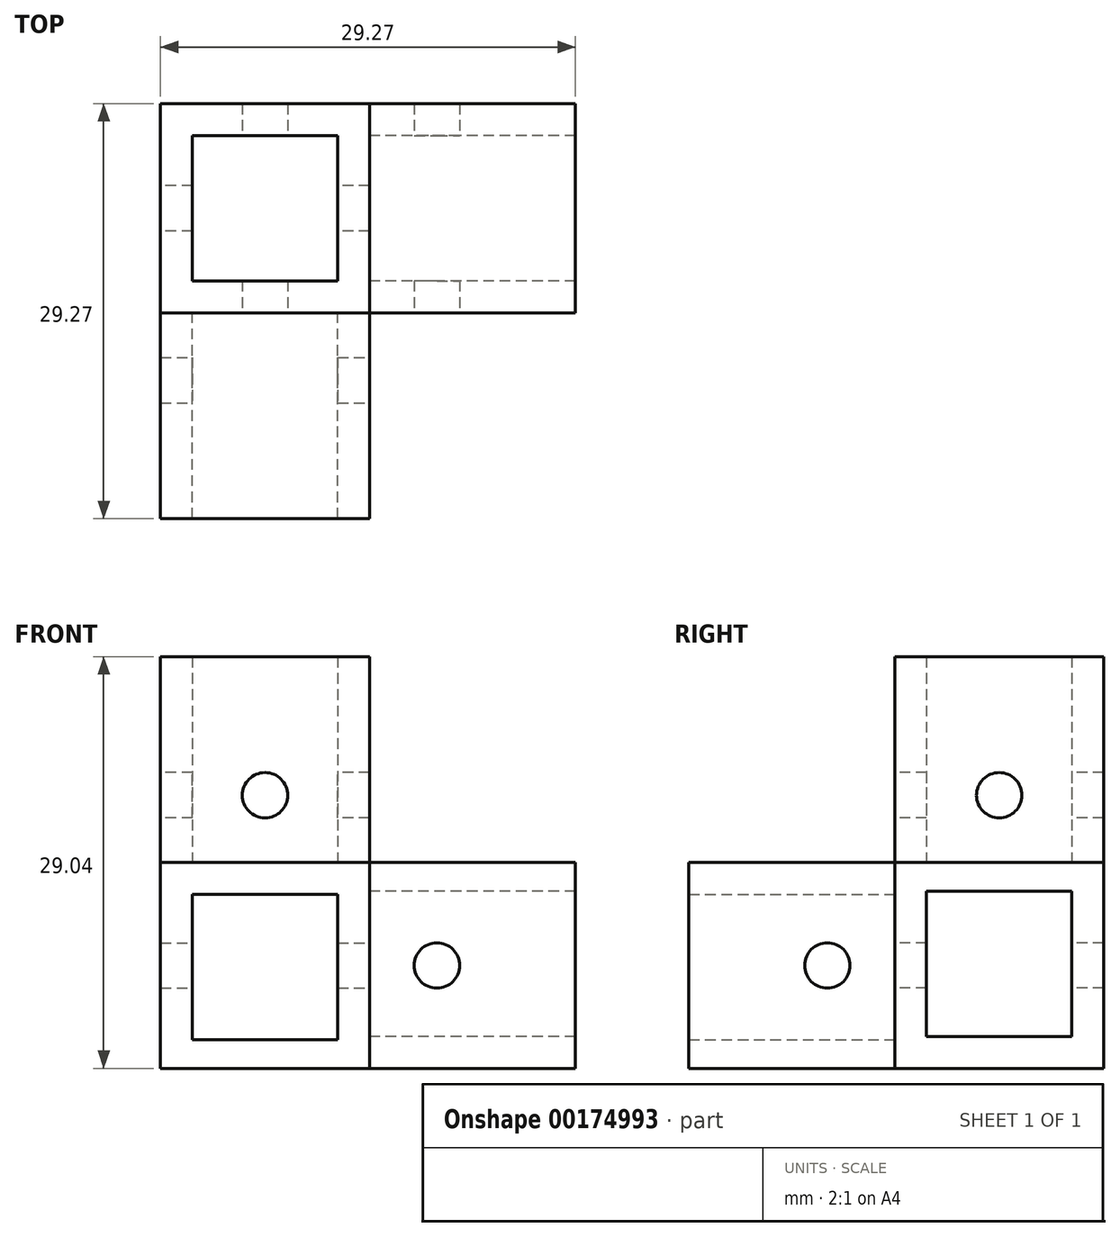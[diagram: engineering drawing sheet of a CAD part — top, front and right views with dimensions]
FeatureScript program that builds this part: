
annotation { "Feature Type Name" : "Feature", "Feature Type Description" : "" }
export const myFeature = defineFeature(function(context is Context, id is Id, definition is map)
    precondition{}
    {
        {
            var Q0;
            Q0=qCreatedBy(makeId("Top.planeOp"),FACE);
            var sketch = newSketch(context, id + "F0", { "sketchPlane" : qUnion([Q0])});
            skLineSegment(sketch, "E0.bottom", {"start": v(0, 0) * mm, "end": v(10.25, 0) * mm});
            skLineSegment(sketch, "E0.top", {"start": v(0, -10.25) * mm, "end": v(10.25, -10.25) * mm});
            skLineSegment(sketch, "E0.left", {"start": v(0, 0) * mm, "end": v(0, -10.25) * mm});
            skLineSegment(sketch, "E0.right", {"start": v(10.25, 0) * mm, "end": v(10.25, -10.25) * mm});
            skLineSegment(sketch, "E1.bottom", {"start": v(-2.25, 2.25) * mm, "end": v(12.5, 2.25) * mm});
            skLineSegment(sketch, "E1.top", {"start": v(-2.25, -12.5) * mm, "end": v(12.5, -12.5) * mm});
            skLineSegment(sketch, "E1.left", {"start": v(-2.25, 2.25) * mm, "end": v(-2.25, -12.5) * mm});
            skLineSegment(sketch, "E1.right", {"start": v(12.5, 2.25) * mm, "end": v(12.5, -12.5) * mm});
            skSolve(sketch);
        }
        {
            var Q0;
            Q0=makeQuery(id+"F0.imprint","IMPRINT",FACE,{"disambiguationData":[TD([[makeQuery(id+"F0.imprint","IMPRINT",EDGE,{"derivedFrom":sQuery(id+"F0.wireOp",EDGE,"E0.bottom")}),1.0]])]});
            extrude(context, id + "F1", {"entities" : qUnion([Q0]), "depth" : 14.52 * mm});
        }
        {
            var Q0;
            Q0=makeQuery(id+"F1.opExtrude","CAP_FACE",FACE,{"disambiguationData":[OSD([sQuery(id+"F0.wireOp",EDGE,"E0.bottom"),sQuery(id+"F0.wireOp",EDGE,"E0.top"),sQuery(id+"F0.wireOp",EDGE,"E0.left"),sQuery(id+"F0.wireOp",EDGE,"E0.right"),sQuery(id+"F0.wireOp",EDGE,"E1.bottom"),sQuery(id+"F0.wireOp",EDGE,"E1.top"),sQuery(id+"F0.wireOp",EDGE,"E1.left"),sQuery(id+"F0.wireOp",EDGE,"E1.right")])],"isStart":true});
            var sketch = newSketch(context, id + "F2", { "sketchPlane" : qUnion([Q0])});
            skLineSegment(sketch, "E2.bottom", {"start": v(-2.25, -2.25) * mm, "end": v(12.5, -2.25) * mm});
            skLineSegment(sketch, "E2.top", {"start": v(-2.25, 12.5) * mm, "end": v(12.5, 12.5) * mm});
            skLineSegment(sketch, "E2.left", {"start": v(-2.25, -2.25) * mm, "end": v(-2.25, 12.5) * mm});
            skLineSegment(sketch, "E2.right", {"start": v(12.5, -2.25) * mm, "end": v(12.5, 12.5) * mm});
            skLineSegment(sketch, "E3.left", {"start": v(-2.25, 12.5) * mm, "end": v(-2.25, -2.25) * mm});
            skLineSegment(sketch, "E3.right", {"start": v(12.5, 12.5) * mm, "end": v(12.5, -2.25) * mm});
            skSolve(sketch);
        }
        {
            var Q0;
            Q0=makeQuery(id+"F2.imprint","IMPRINT",FACE,{"disambiguationData":[TD([[makeQuery(id+"F2.imprint","IMPRINT",EDGE,{"derivedFrom":sQuery(id+"F2.wireOp",EDGE,"E2.top")}),-1.0]])]});
            var Q1;
            Q1=makeQuery(id+"F2.imprint","IMPRINT",FACE,{"disambiguationData":[TD([[makeQuery(id+"F2.imprint","IMPRINT",EDGE,{"derivedFrom":makeQuery(id+"F1.opExtrude","CAP_EDGE",EDGE,{"disambiguationData":[OSD([sQuery(id+"F0.wireOp",EDGE,"E0.bottom")])],"isStart":true})}),1.0]])]});
            extrude(context, id + "F3", {"entities" : qUnion([Q0, Q1]), "operationType" : NewBodyOperationType.ADD, "depth" : 14.52 * mm});
        }
        {
            var Q0;
            Q0=makeQuery(id+"F3.boolean.opBoolean","MERGE",FACE,{"derivedFrom":[makeQuery(id+"F1.opExtrude","SWEPT_FACE",FACE,{"disambiguationData":[OSD([sQuery(id+"F0.wireOp",EDGE,"E1.top")])]}),makeQuery(id+"F3.opExtrude","SWEPT_FACE",FACE,{"disambiguationData":[OSD([sQuery(id+"F2.wireOp",EDGE,"E2.top")])]})]});
            var sketch = newSketch(context, id + "F4", { "sketchPlane" : qUnion([Q0])});
            skLineSegment(sketch, "E4.bottom", {"start": v(-2.25, 0) * mm, "end": v(12.5, 0) * mm});
            skLineSegment(sketch, "E4.top", {"start": v(-2.25, -14.52) * mm, "end": v(12.5, -14.52) * mm});
            skLineSegment(sketch, "E4.left", {"start": v(-2.25, 0) * mm, "end": v(-2.25, -14.52) * mm});
            skLineSegment(sketch, "E4.right", {"start": v(12.5, 0) * mm, "end": v(12.5, -14.52) * mm});
            skLineSegment(sketch, "E5.left", {"start": v(0, -2.25) * mm, "end": v(0, -12.27) * mm});
            skLineSegment(sketch, "E5.right", {"start": v(10.25, -2.25) * mm, "end": v(10.25, -12.27) * mm});
            skLineSegment(sketch, "E6.bottom", {"start": v(0, -2.25) * mm, "end": v(10.25, -2.25) * mm});
            skLineSegment(sketch, "E6.top", {"start": v(0, -12.5) * mm, "end": v(10.25, -12.5) * mm});
            skLineSegment(sketch, "E6.left", {"start": v(0, -2.25) * mm, "end": v(0, -12.5) * mm});
            skLineSegment(sketch, "E6.right", {"start": v(10.25, -2.25) * mm, "end": v(10.25, -12.5) * mm});
            skSolve(sketch);
        }
        {
            var Q0;
            Q0=makeQuery(id+"F4.imprint","IMPRINT",FACE,{"disambiguationData":[TD([[makeQuery(id+"F4.imprint","IMPRINT",EDGE,{"derivedFrom":sQuery(id+"F4.wireOp",EDGE,"E4.bottom")}),-1.0]])]});
            extrude(context, id + "F5", {"entities" : qUnion([Q0]), "operationType" : NewBodyOperationType.ADD, "depth" : 14.52 * mm});
        }
        {
            var Q0;
            Q0=makeQuery(id+"F5.boolean.opBoolean","MERGE",FACE,{"derivedFrom":[makeQuery(id+"F3.boolean.opBoolean","MERGE",FACE,{"derivedFrom":[makeQuery(id+"F1.opExtrude","SWEPT_FACE",FACE,{"disambiguationData":[OSD([sQuery(id+"F0.wireOp",EDGE,"E1.right")])]}),makeQuery(id+"F3.opExtrude","SWEPT_FACE",FACE,{"disambiguationData":[OSD([sQuery(id+"F2.wireOp",EDGE,"E3.right")])]})]}),makeQuery(id+"F5.opExtrude","SWEPT_FACE",FACE,{"disambiguationData":[OSD([sQuery(id+"F4.wireOp",EDGE,"E4.right")])]})]});
            var sketch = newSketch(context, id + "F6", { "sketchPlane" : qUnion([Q0])});
            skLineSegment(sketch, "E7.bottom", {"start": v(2.25, -14.52) * mm, "end": v(-12.5, -14.52) * mm});
            skLineSegment(sketch, "E7.top", {"start": v(2.25, 0) * mm, "end": v(-12.5, 0) * mm});
            skLineSegment(sketch, "E7.left", {"start": v(2.25, -14.52) * mm, "end": v(2.25, 0) * mm});
            skLineSegment(sketch, "E7.right", {"start": v(-12.5, -14.52) * mm, "end": v(-12.5, 0) * mm});
            skLineSegment(sketch, "E8.bottom", {"start": v(-10.25, -2.02) * mm, "end": v(0, -2.02) * mm});
            skLineSegment(sketch, "E8.top", {"start": v(-10.25, -12.27) * mm, "end": v(0, -12.27) * mm});
            skLineSegment(sketch, "E8.left", {"start": v(-10.25, -2.02) * mm, "end": v(-10.25, -12.27) * mm});
            skLineSegment(sketch, "E8.right", {"start": v(0, -2.02) * mm, "end": v(0, -12.27) * mm});
            skSolve(sketch);
        }
        {
            var Q0;
            Q0=makeQuery(id+"F6.imprint","IMPRINT",FACE,{"disambiguationData":[TD([[makeQuery(id+"F6.imprint","IMPRINT",EDGE,{"derivedFrom":sQuery(id+"F6.wireOp",EDGE,"E7.bottom")}),-1.0]])]});
            extrude(context, id + "F7", {"entities" : qUnion([Q0]), "operationType" : NewBodyOperationType.ADD, "depth" : 14.52 * mm});
        }
        {
            var Q0;
            Q0=makeQuery(id+"F7.opExtrude","SWEPT_FACE",FACE,{"disambiguationData":[OSD([sQuery(id+"F6.wireOp",EDGE,"E7.right")])]});
            var sketch = newSketch(context, id + "F8", { "sketchPlane" : qUnion([Q0])});
            skCircle(sketch, "E9", {"center": v(17.25, -7.26) * mm, "radius": 1.6 * mm});
            skPoint(sketch, "E9.centerSnap0", {"position": v(27.02, -7.26) * mm});
            skPoint(sketch, "E9.perimeterSnap0", {"position": v(27.02, -7.26) * mm});
            skPoint(sketch, "E9.perimeterSnap1", {"position": v(19.76, 0) * mm});
            skSolve(sketch);
        }
        {
            var Q0;
            Q0=makeQuery(id+"F8.imprint","IMPRINT",FACE,{"disambiguationData":[TD([[makeQuery(id+"F8.imprint","IMPRINT",EDGE,{"derivedFrom":sQuery(id+"F8.wireOp",EDGE,"E9")}),1.0]])]});
            extrude(context, id + "F9", {"entities" : qUnion([Q0]), "operationType" : NewBodyOperationType.REMOVE, "oppositeDirection" : true, "depth" : 25.4 * mm});
        }
        {
            var Q0;
            {var subQ0=sQuery(id+"F4.wireOp",EDGE,"E4.right");var subQ1=makeQuery(id+"F5.opExtrude","SWEPT_FACE",FACE,{"disambiguationData":[OSD([subQ0])]});var subQ2=sQuery(id+"F4.wireOp",EDGE,"E4.top");var subQ4=makeQuery(id+"F1.opExtrude","SWEPT_FACE",FACE,{"disambiguationData":[OSD([sQuery(id+"F0.wireOp",EDGE,"E1.right")])]});var subQ5=sQuery(id+"F2.wireOp",EDGE,"E3.right");var subQ6=makeQuery(id+"F3.opExtrude","SWEPT_FACE",FACE,{"disambiguationData":[OSD([subQ5])]});Q0=makeQuery(id+"F7.boolean.opBoolean","SPLIT",FACE,{"disambiguationData":[TD([makeQuery(id+"F5.opExtrude","SWEPT_FACE",FACE,{"disambiguationData":[OSD([subQ2])]})])],"derivedFrom":makeQuery(id+"F5.boolean.opBoolean","MERGE",FACE,{"derivedFrom":[makeQuery(id+"F3.boolean.opBoolean","MERGE",FACE,{"derivedFrom":[subQ4,subQ6]}),subQ1]})});}
            var sketch = newSketch(context, id + "F10", { "sketchPlane" : qUnion([Q0])});
            skCircle(sketch, "E10", {"center": v(-17.25, -7.26) * mm, "radius": 1.6 * mm});
            skPoint(sketch, "E10.centerSnap0", {"position": v(-12.5, -7.26) * mm});
            skSolve(sketch);
        }
        {
            var Q0;
            Q0 = qSketchRegion(id + "F10", true);
            extrude(context, id + "F11", {"entities" : qUnion([Q0]), "operationType" : NewBodyOperationType.REMOVE, "oppositeDirection" : true, "depth" : 25.4 * mm});
        }
        {
            var Q0;
            Q0=makeQuery(id+"F5.boolean.opBoolean","MERGE",FACE,{"derivedFrom":[makeQuery(id+"F3.boolean.opBoolean","MERGE",FACE,{"derivedFrom":[makeQuery(id+"F1.opExtrude","SWEPT_FACE",FACE,{"disambiguationData":[OSD([sQuery(id+"F0.wireOp",EDGE,"E1.left")])]}),makeQuery(id+"F3.opExtrude","SWEPT_FACE",FACE,{"disambiguationData":[OSD([sQuery(id+"F2.wireOp",EDGE,"E3.left")])]})]}),makeQuery(id+"F5.opExtrude","SWEPT_FACE",FACE,{"disambiguationData":[OSD([sQuery(id+"F4.wireOp",EDGE,"E4.left")])]})]});
            var sketch = newSketch(context, id + "F12", { "sketchPlane" : qUnion([Q0])});
            skCircle(sketch, "E11", {"center": v(5.12, 4.75) * mm, "radius": 1.6 * mm});
            skPoint(sketch, "E11.centerSnap0", {"position": v(5.12, 14.52) * mm});
            skSolve(sketch);
        }
        {
            var Q0;
            Q0=makeQuery(id+"F12.imprint","IMPRINT",FACE,{"disambiguationData":[TD([[makeQuery(id+"F12.imprint","IMPRINT",EDGE,{"derivedFrom":sQuery(id+"F12.wireOp",EDGE,"E11")}),1.0]])]});
            extrude(context, id + "F13", {"entities" : qUnion([Q0]), "operationType" : NewBodyOperationType.REMOVE, "oppositeDirection" : true, "depth" : 25.4 * mm});
        }
        {
            var Q0;
            {var subQ1=sQuery(id+"F0.wireOp",EDGE,"E1.left");var subQ2=sQuery(id+"F0.wireOp",EDGE,"E1.top");Q0=makeQuery(id+"F5.boolean.opBoolean","SPLIT",FACE,{"disambiguationData":[TD([makeQuery(id+"F1.opExtrude","SWEPT_FACE",FACE,{"disambiguationData":[OSD([subQ1])]})])],"derivedFrom":makeQuery(id+"F3.boolean.opBoolean","MERGE",FACE,{"derivedFrom":[makeQuery(id+"F1.opExtrude","SWEPT_FACE",FACE,{"disambiguationData":[OSD([subQ2])]}),makeQuery(id+"F3.opExtrude","SWEPT_FACE",FACE,{"disambiguationData":[OSD([sQuery(id+"F2.wireOp",EDGE,"E2.top")])]})]})});}
            var sketch = newSketch(context, id + "F14", { "sketchPlane" : qUnion([Q0])});
            skCircle(sketch, "E12", {"center": v(5.13, 4.75) * mm, "radius": 1.6 * mm});
            skPoint(sketch, "E12.centerSnap0", {"position": v(5.13, 14.52) * mm});
            skSolve(sketch);
        }
        {
            var Q0;
            Q0=makeQuery(id+"F14.imprint","IMPRINT",FACE,{"disambiguationData":[TD([[makeQuery(id+"F14.imprint","IMPRINT",EDGE,{"derivedFrom":sQuery(id+"F14.wireOp",EDGE,"E12")}),1.0]])]});
            extrude(context, id + "F15", {"entities" : qUnion([Q0]), "operationType" : NewBodyOperationType.REMOVE, "oppositeDirection" : true, "depth" : 25.4 * mm});
        }
    });
